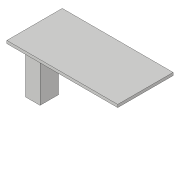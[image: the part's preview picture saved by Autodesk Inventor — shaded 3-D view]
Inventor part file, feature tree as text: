
AUTODESK INVENTOR PART (.ipt)
format: ipt  version: 2019 (Build 230136000, 136)  size: 102,400 bytes
history: native  units: in
note: dims shown in document units (in); Inventor stores cm internally (conversion verified against a paired STEP export)
features: sketch x5, extrude x3
ambient origin geometry x8: Origin, YZ Plane, XZ Plane, XY Plane, X Axis, Y Axis, Z Axis, Center Point
bodies: Solid1 (feature_tree)
feature tree (8):
  extrude  "Extrusion1"  Depth=39.3701in
  sketch  "Sketch2"  dims[d3=1.9685in d4=0.0in d5=12.9921in]
  extrude  "Extrusion2"  Depth=1.9685in
  extrude  "Extrusion3"  Depth=39.3701in
  sketch  "Sketch5"  dims[d10=3.937in d11=0.0in]
  sketch  "Sketch1"  dims[d1=78.7402in d2=39.3701in]
  sketch  "Sketch3"  dims[d6=39.3701in d7=0.0in d8=6.5748in]
  sketch  "Sketch4"  dims[d9=7.874in]
